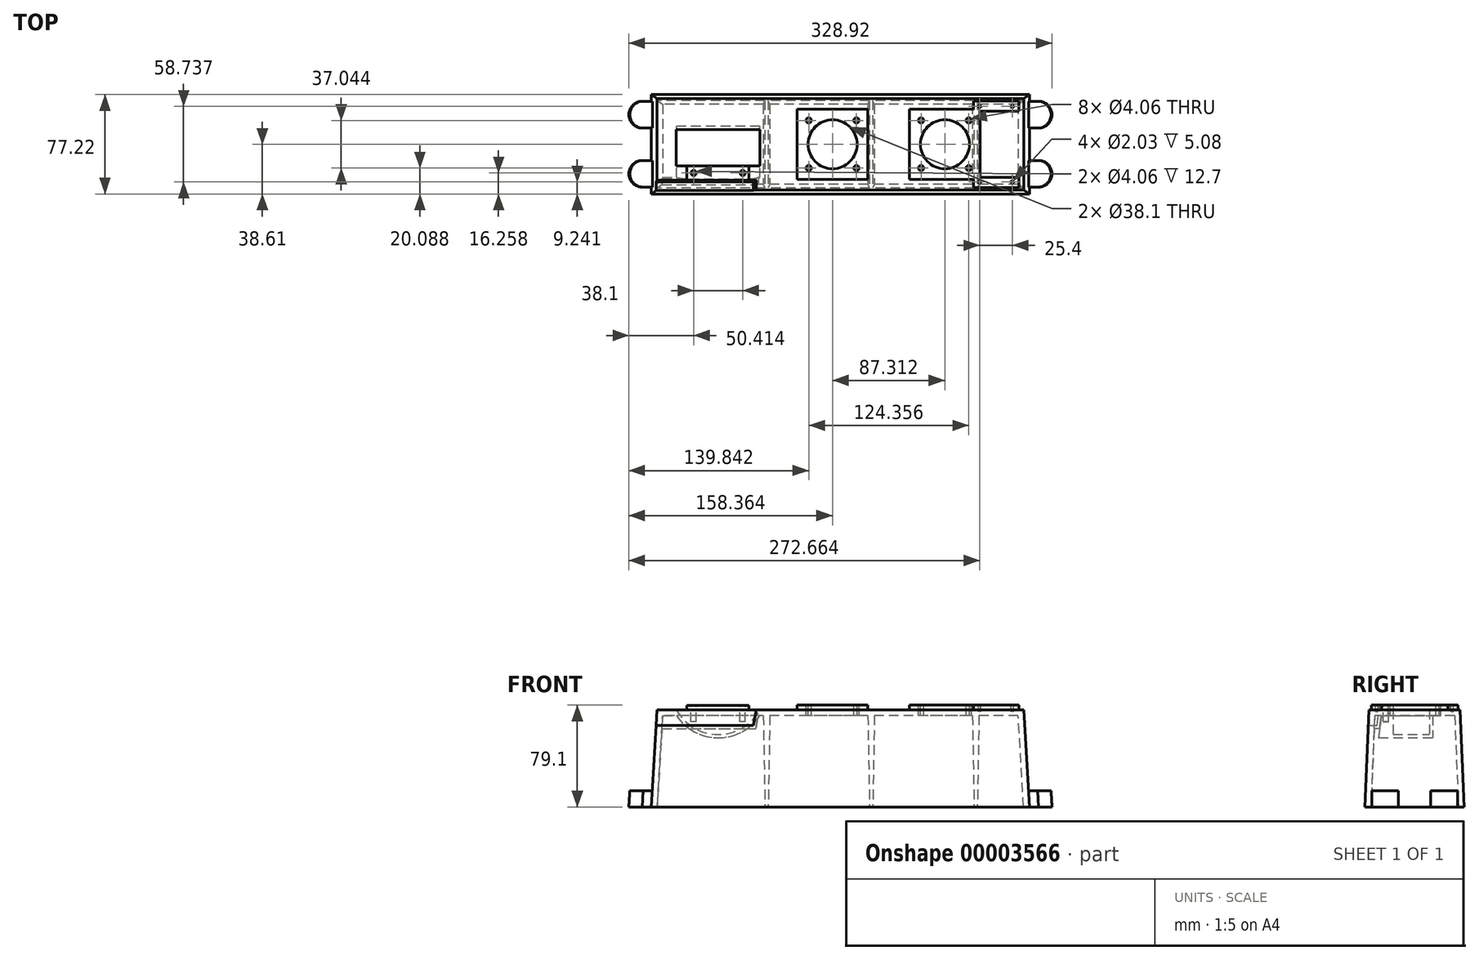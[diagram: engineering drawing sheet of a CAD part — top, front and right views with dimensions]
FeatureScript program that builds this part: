
annotation { "Feature Type Name" : "Feature", "Feature Type Description" : "" }
export const myFeature = defineFeature(function(context is Context, id is Id, definition is map)
    precondition{}
    {
        {
            var Q0;
            Q0=qCreatedBy(makeId("Top.planeOp"),FACE);
            cPlane(context, id + "F0", {"entities" : qUnion([Q0]), "cplaneType" : CPlaneType.OFFSET, "offset" : 75.6 * mm, "width" : 152.4 * mm, "height" : 152.4 * mm});
        }
        {
            var Q0;
            Q0=qCreatedBy(makeId("Top.planeOp"),FACE);
            var sketch = newSketch(context, id + "F1", { "sketchPlane" : qUnion([Q0])});
            skLineSegment(sketch, "E0.rect.bottom", {"start": v(146.94, 38.6) * mm, "end": v(-146.94, 38.6) * mm});
            skLineSegment(sketch, "E0.rect.top", {"start": v(146.94, -38.6) * mm, "end": v(-146.94, -38.6) * mm});
            skLineSegment(sketch, "E0.rect.left", {"start": v(146.94, 38.6) * mm, "end": v(146.94, -38.6) * mm});
            skLineSegment(sketch, "E0.rect.right", {"start": v(-146.94, 38.6) * mm, "end": v(-146.94, -38.6) * mm});
            skPoint(sketch, "E0.rect.middle", {"position": v(0, 0) * mm});
            skSolve(sketch);
        }
        {
            var Q0;
            Q0=qCreatedBy(id+"F0.planeOp",FACE);
            var sketch = newSketch(context, id + "F2", { "sketchPlane" : qUnion([Q0])});
            skLineSegment(sketch, "E1.rect.bottom", {"start": v(142.5, 35.43) * mm, "end": v(-142.5, 35.43) * mm});
            skLineSegment(sketch, "E1.rect.top", {"start": v(142.5, -35.43) * mm, "end": v(-142.5, -35.43) * mm});
            skLineSegment(sketch, "E1.rect.left", {"start": v(142.5, 35.43) * mm, "end": v(142.5, -35.43) * mm});
            skLineSegment(sketch, "E1.rect.right", {"start": v(-142.5, 35.43) * mm, "end": v(-142.5, -35.43) * mm});
            skPoint(sketch, "E1.rect.middle", {"position": v(0, 0) * mm});
            skSolve(sketch);
        }
        {
            var Q0;
            Q0=makeQuery(id+"F1.imprint","IMPRINT",FACE,{"disambiguationData":[TD([[makeQuery(id+"F1.imprint","IMPRINT",EDGE,{"derivedFrom":sQuery(id+"F1.wireOp",EDGE,"E0.rect.bottom")}),1.0]])]});
            var Q1;
            Q1=makeQuery(id+"F2.imprint","IMPRINT",FACE,{"disambiguationData":[TD([[makeQuery(id+"F2.imprint","IMPRINT",EDGE,{"derivedFrom":sQuery(id+"F2.wireOp",EDGE,"E1.rect.bottom")}),1.0]])]});
            loft(context, id + "F3", {"sheetProfilesArray" : [{ "sheetProfileEntities" : qUnion([Q0]) }, { "sheetProfileEntities" : qUnion([Q1]) }]});
        }
        {
            var Q0;
            Q0=makeQuery(id+"F3.opLoft","CAP_FACE",FACE,{"disambiguationData":[OSD([makeQuery(id+"F1.imprint","IMPRINT",FACE,{"disambiguationData":[TD([[makeQuery(id+"F1.imprint","IMPRINT",EDGE,{"derivedFrom":sQuery(id+"F1.wireOp",EDGE,"E0.rect.bottom")}),1.0]])]})])],"isStart":true});
            shell(context, id + "F4", {"entities" : qUnion([Q0]), "thickness" : 4.57 * mm});
        }
        {
            var Q0;
            Q0=makeQuery(id+"F3.opLoft","SWEPT_FACE",FACE,{"disambiguationData":[OSD([sQuery(id+"F1.wireOp",EDGE,"E0.rect.bottom"),sQuery(id+"F1.wireOp",EDGE,"E0.rect.top"),sQuery(id+"F1.wireOp",EDGE,"E0.rect.right"),sQuery(id+"F2.wireOp",EDGE,"E1.rect.bottom"),sQuery(id+"F2.wireOp",EDGE,"E1.rect.top"),sQuery(id+"F2.wireOp",EDGE,"E1.rect.right")])]});
            var sketch = newSketch(context, id + "F5", { "sketchPlane" : qUnion([Q0])});
            skLineSegment(sketch, "E2", {"start": v(-22.99, -8.62) * mm, "end": v(-22.99, 4.08) * mm});
            skLineSegment(sketch, "E3", {"start": v(22.99, -8.62) * mm, "end": v(22.99, 4.08) * mm});
            skSolve(sketch);
        }
        {
            var Q0;
            Q0=qCreatedBy(makeId("Top.planeOp"),FACE);
            var sketch = newSketch(context, id + "F6", { "sketchPlane" : qUnion([Q0])});
            skLineSegment(sketch, "E4.bottom", {"start": v(-146.94, 33.4) * mm, "end": v(-154.05, 33.4) * mm});
            skLineSegment(sketch, "E4.top", {"start": v(-146.94, 12.57) * mm, "end": v(-154.05, 12.57) * mm});
            skLineSegment(sketch, "E4.left", {"start": v(-146.94, 33.4) * mm, "end": v(-146.94, 12.57) * mm});
            skLineSegment(sketch, "E4.right", {"start": v(-164.47, 22.99) * mm, "end": v(-164.47, 22.99) * mm});
            skLineSegment(sketch, "E5.bottom", {"start": v(-146.94, -12.57) * mm, "end": v(-154.05, -12.57) * mm});
            skLineSegment(sketch, "E5.top", {"start": v(-146.94, -33.4) * mm, "end": v(-154.05, -33.4) * mm});
            skLineSegment(sketch, "E5.left", {"start": v(-146.94, -12.57) * mm, "end": v(-146.94, -33.4) * mm});
            skLineSegment(sketch, "E5.right", {"start": v(-164.47, -22.99) * mm, "end": v(-164.47, -22.99) * mm});
            skPoint(sketch, "E6.visualSharp", {"position": v(-164.47, 33.4) * mm});
            skArc(sketch, "E6.filletArc", {"start": v(-154.05, 33.4) * mm, "mid": v(-161.41, 30.35) * mm, "end": v(-164.47, 22.99) * mm});
            skPoint(sketch, "E7.visualSharp", {"position": v(-164.47, 12.57) * mm});
            skArc(sketch, "E7.filletArc", {"start": v(-164.47, 22.99) * mm, "mid": v(-161.41, 15.62) * mm, "end": v(-154.05, 12.57) * mm});
            skPoint(sketch, "E8.visualSharp", {"position": v(-164.47, -12.57) * mm});
            skArc(sketch, "E8.filletArc", {"start": v(-154.05, -12.57) * mm, "mid": v(-161.41, -15.62) * mm, "end": v(-164.47, -22.99) * mm});
            skPoint(sketch, "E9.visualSharp", {"position": v(-164.47, -33.4) * mm});
            skArc(sketch, "E9.filletArc", {"start": v(-164.47, -22.99) * mm, "mid": v(-161.41, -30.35) * mm, "end": v(-154.05, -33.4) * mm});
            skSolve(sketch);
        }
        {
            var Q0;
            Q0=makeQuery(id+"F6.imprint","IMPRINT",FACE,{"disambiguationData":[TD([[makeQuery(id+"F6.imprint","IMPRINT",EDGE,{"derivedFrom":sQuery(id+"F6.wireOp",EDGE,"E4.bottom")}),1.0]])]});
            var Q1;
            Q1=makeQuery(id+"F6.imprint","IMPRINT",FACE,{"disambiguationData":[TD([[makeQuery(id+"F6.imprint","IMPRINT",EDGE,{"derivedFrom":sQuery(id+"F6.wireOp",EDGE,"E5.bottom")}),1.0]])]});
            var Q2;
            Q2=sQuery(id+"F5.wireOp",EDGE,"E2");
            sweep(context, id + "F7", {"operationType" : NewBodyOperationType.ADD, "profiles" : qUnion([Q0, Q1]), "path" : qUnion([Q2])});
        }
        {
            var Q0;
            Q0=makeQuery(id+"F3.opLoft","SWEPT_BODY",BODY,{"disambiguationData":[OSD([makeQuery(id+"F1.imprint","IMPRINT",FACE,{"disambiguationData":[TD([[makeQuery(id+"F1.imprint","IMPRINT",EDGE,{"derivedFrom":sQuery(id+"F1.wireOp",EDGE,"E0.rect.bottom")}),1.0]])]}),makeQuery(id+"F2.imprint","IMPRINT",FACE,{"disambiguationData":[TD([[makeQuery(id+"F2.imprint","IMPRINT",EDGE,{"derivedFrom":sQuery(id+"F2.wireOp",EDGE,"E1.rect.bottom")}),1.0]])]})])]});
            var Q1;
            Q1=qCreatedBy(makeId("Right.planeOp"),FACE);
            mirror(context, id + "F8", {"entities" : qUnion([Q0]), "mirrorPlane" : qUnion([Q1])});
        }
        {
            var Q0;
            Q0=qCreatedBy(id+"F0.planeOp",FACE);
            cPlane(context, id + "F9", {"entities" : qUnion([Q0]), "cplaneType" : CPlaneType.OFFSET, "offset" : 12.14 * mm, "oppositeDirection" : true, "width" : 152.4 * mm, "height" : 152.4 * mm});
        }
        {
            var Q0;
            Q0=qCreatedBy(id+"F9.planeOp",FACE);
            cPlane(context, id + "F10", {"entities" : qUnion([Q0]), "cplaneType" : CPlaneType.OFFSET, "offset" : 2.54 * mm, "oppositeDirection" : true, "width" : 152.4 * mm, "height" : 152.4 * mm});
        }
        {
            var Q0;
            Q0=qCreatedBy(id+"F10.planeOp",FACE);
            var sketch = newSketch(context, id + "F11", { "sketchPlane" : qUnion([Q0])});
            skLineSegment(sketch, "E10.bottom", {"start": v(-143.36, -27.16) * mm, "end": v(-65.89, -27.16) * mm});
            skLineSegment(sketch, "E10.top", {"start": v(-143.36, -36.05) * mm, "end": v(-65.89, -36.05) * mm});
            skLineSegment(sketch, "E10.left", {"start": v(-143.36, -27.16) * mm, "end": v(-143.36, -36.05) * mm});
            skLineSegment(sketch, "E10.right", {"start": v(-65.89, -27.16) * mm, "end": v(-65.89, -36.05) * mm});
            skSolve(sketch);
        }
        {
            var Q0;
            Q0=makeQuery(id+"F3.opLoft","CAP_FACE",FACE,{"disambiguationData":[OSD([makeQuery(id+"F2.imprint","IMPRINT",FACE,{"disambiguationData":[TD([[makeQuery(id+"F2.imprint","IMPRINT",EDGE,{"derivedFrom":sQuery(id+"F2.wireOp",EDGE,"E1.rect.bottom")}),1.0]])]})])],"isStart":true});
            var sketch = newSketch(context, id + "F12", { "sketchPlane" : qUnion([Q0])});
            skLineSegment(sketch, "E11.bottom", {"start": v(-63, -35.43) * mm, "end": v(-142.5, -35.43) * mm});
            skLineSegment(sketch, "E11.top", {"start": v(-63, -25.27) * mm, "end": v(-142.5, -25.27) * mm});
            skLineSegment(sketch, "E11.left", {"start": v(-63, -35.43) * mm, "end": v(-63, -25.27) * mm});
            skLineSegment(sketch, "E11.right", {"start": v(-142.5, -35.43) * mm, "end": v(-142.5, -25.27) * mm});
            skSolve(sketch);
        }
        {
            var Q2;
            Q2=makeQuery(id+"F12.imprint","IMPRINT",FACE,{"disambiguationData":[TD([[makeQuery(id+"F12.imprint","IMPRINT",EDGE,{"derivedFrom":sQuery(id+"F12.wireOp",EDGE,"E11.bottom")}),1.0]])]});
            var Q3;
            Q3 = qSketchRegion(id + "F11", true);
            loft(context, id + "F13", {"operationType" : NewBodyOperationType.ADD, "sheetProfilesArray" : [{ "sheetProfileEntities" : qUnion([Q2]) }, { "sheetProfileEntities" : qUnion([Q3]) }]});
        }
        {
            var Q0;
            Q0=makeQuery(id+"F3.opLoft","CAP_FACE",FACE,{"disambiguationData":[OSD([makeQuery(id+"F2.imprint","IMPRINT",FACE,{"disambiguationData":[TD([[makeQuery(id+"F2.imprint","IMPRINT",EDGE,{"derivedFrom":sQuery(id+"F2.wireOp",EDGE,"E1.rect.bottom")}),1.0]])]})])],"isStart":true});
            var sketch = newSketch(context, id + "F14", { "sketchPlane" : qUnion([Q0])});
            skLineSegment(sketch, "E12.bottom", {"start": v(-65.53, -27.81) * mm, "end": v(-150.84, -27.81) * mm});
            skLineSegment(sketch, "E12.top", {"start": v(-65.53, -43.06) * mm, "end": v(-150.84, -43.06) * mm});
            skLineSegment(sketch, "E12.left", {"start": v(-65.53, -27.81) * mm, "end": v(-65.53, -43.06) * mm});
            skLineSegment(sketch, "E12.right", {"start": v(-150.84, -27.81) * mm, "end": v(-150.84, -43.06) * mm});
            skSolve(sketch);
        }
        {
            var Q0;
            Q0=qCreatedBy(id+"F9.planeOp",FACE);
            var sketch = newSketch(context, id + "F15", { "sketchPlane" : qUnion([Q0])});
            skLineSegment(sketch, "E13.bottom", {"start": v(-67.56, -29.08) * mm, "end": v(-150.57, -29.08) * mm});
            skLineSegment(sketch, "E13.top", {"start": v(-67.56, -49.34) * mm, "end": v(-150.57, -49.34) * mm});
            skLineSegment(sketch, "E13.left", {"start": v(-67.56, -29.08) * mm, "end": v(-67.56, -49.34) * mm});
            skLineSegment(sketch, "E13.right", {"start": v(-150.57, -29.08) * mm, "end": v(-150.57, -49.34) * mm});
            skSolve(sketch);
        }
        {
            var Q1;
            {var subQ3=sQuery(id+"F14.wireOp",EDGE,"E12.left");var subQ7=sQuery(id+"F14.wireOp",EDGE,"E12.bottom");var subQ9=makeQuery(id+"F14.imprint","INTERSECT",VERTEX,{"derivedFrom":[subQ7,subQ3]});Q1=makeQuery(id+"F14.imprint","IMPRINT",FACE,{"disambiguationData":[TD([[makeQuery(id+"F14.imprint","IMPRINT",EDGE,{"disambiguationData":[TD([[subQ9,-1.0]])],"derivedFrom":subQ7}),1.0]])]});}
            var Q2;
            Q2=makeQuery(id+"F15.imprint","IMPRINT",FACE,{"disambiguationData":[TD([[makeQuery(id+"F15.imprint","IMPRINT",EDGE,{"derivedFrom":sQuery(id+"F15.wireOp",EDGE,"E13.bottom")}),1.0]])]});
            loft(context, id + "F16", {"operationType" : NewBodyOperationType.REMOVE, "sheetProfilesArray" : [{ "sheetProfileEntities" : qUnion([Q1]) }, { "sheetProfileEntities" : qUnion([Q2]) }]});
        }
        {
            var Q0;
            Q0=makeQuery(id+"F3.opLoft","CAP_FACE",FACE,{"disambiguationData":[OSD([makeQuery(id+"F2.imprint","IMPRINT",FACE,{"disambiguationData":[TD([[makeQuery(id+"F2.imprint","IMPRINT",EDGE,{"derivedFrom":sQuery(id+"F2.wireOp",EDGE,"E1.rect.bottom")}),1.0]])]})])],"isStart":true});
            var sketch = newSketch(context, id + "F17", { "sketchPlane" : qUnion([Q0])});
            skLineSegment(sketch, "E14.bottom", {"start": v(-119.38, -27.81) * mm, "end": v(-71.12, -27.81) * mm});
            skLineSegment(sketch, "E14.top", {"start": v(-119.38, -16.9) * mm, "end": v(-71.12, -16.9) * mm});
            skLineSegment(sketch, "E14.left", {"start": v(-119.38, -27.81) * mm, "end": v(-119.38, -16.9) * mm});
            skLineSegment(sketch, "E14.right", {"start": v(-71.12, -27.81) * mm, "end": v(-71.12, -16.9) * mm});
            skSolve(sketch);
        }
        {
            var Q0;
            Q0 = qSketchRegion(id + "F17", true);
            extrude(context, id + "F18", {"entities" : qUnion([Q0]), "operationType" : NewBodyOperationType.ADD, "depth" : 3.2 * mm});
        }
        {
            var Q0;
            Q0=makeQuery(id+"F3.opLoft","CAP_FACE",FACE,{"disambiguationData":[OSD([makeQuery(id+"F2.imprint","IMPRINT",FACE,{"disambiguationData":[TD([[makeQuery(id+"F2.imprint","IMPRINT",EDGE,{"derivedFrom":sQuery(id+"F2.wireOp",EDGE,"E1.rect.bottom")}),1.0]])]})])],"isStart":true});
            var sketch = newSketch(context, id + "F19", { "sketchPlane" : qUnion([Q0])});
            skLineSegment(sketch, "E15.bottom", {"start": v(-127.5, -16.9) * mm, "end": v(-62.48, -16.9) * mm});
            skLineSegment(sketch, "E15.top", {"start": v(-127.5, 11.56) * mm, "end": v(-62.48, 11.56) * mm});
            skLineSegment(sketch, "E15.left", {"start": v(-127.5, -16.9) * mm, "end": v(-127.5, 11.56) * mm});
            skLineSegment(sketch, "E15.right", {"start": v(-62.48, -16.9) * mm, "end": v(-62.48, 11.56) * mm});
            skSolve(sketch);
        }
        {
            var Q0;
            Q0=sQuery(id+"F19.wireOp",EDGE,"E15.top");
            cPlane(context, id + "F20", {"entities" : qUnion([Q0]), "cplaneType" : CPlaneType.LINE_ANGLE, "offset" : 152.4 * mm, "angle" : 0 * degree, "width" : 152.4 * mm, "height" : 152.4 * mm});
        }
        {
            var Q0;
            Q0=qCreatedBy(id+"F20.planeOp",FACE);
            var sketch = newSketch(context, id + "F21", { "sketchPlane" : qUnion([Q0])});
            skArc(sketch, "E16", {"start": v(59.94, 75.6) * mm, "mid": v(95, 53.76) * mm, "end": v(130.05, 75.6) * mm});
            skLineSegment(sketch, "E17", {"start": v(59.94, 75.6) * mm, "end": v(130.05, 75.6) * mm});
            skSolve(sketch);
        }
        {
            var Q0;
            Q0 = qSketchRegion(id + "F21", true);
            var Q1;
            Q1=makeQuery(id+"F13.opLoft","SWEPT_FACE",FACE,{"disambiguationData":[OSD([sQuery(id+"F2.wireOp",EDGE,"E1.rect.bottom"),sQuery(id+"F2.wireOp",EDGE,"E1.rect.top"),sQuery(id+"F2.wireOp",EDGE,"E1.rect.right"),sQuery(id+"F11.wireOp",EDGE,"E10.bottom"),sQuery(id+"F11.wireOp",EDGE,"E10.left"),sQuery(id+"F11.wireOp",EDGE,"E10.right"),sQuery(id+"F12.wireOp",EDGE,"E11.top"),sQuery(id+"F12.wireOp",EDGE,"E11.left"),sQuery(id+"F12.wireOp",EDGE,"E11.right")])]});
            extrude(context, id + "F22", {"entities" : qUnion([Q0]), "operationType" : NewBodyOperationType.ADD, "endBound" : BoundingType.UP_TO_SURFACE, "oppositeDirection" : true, "endBoundEntityFace" : qUnion([Q1]), "depth" : 25.4 * mm, "hasSecondDirection" : true, "secondDirectionOppositeDirection" : false, "secondDirectionDepth" : 2.54 * mm});
        }
        {
            var Q0;
            Q0=qCreatedBy(id+"F20.planeOp",FACE);
            var sketch = newSketch(context, id + "F23", { "sketchPlane" : qUnion([Q0])});
            skArc(sketch, "E18", {"start": v(62.48, 75.6) * mm, "mid": v(95, 56.3) * mm, "end": v(127.5, 75.6) * mm});
            skLineSegment(sketch, "E19", {"start": v(62.48, 75.6) * mm, "end": v(127.5, 75.6) * mm});
            skSolve(sketch);
        }
        {
            var Q0;
            Q0 = qSketchRegion(id + "F23", true);
            var Q1;
            Q1=makeQuery(id+"F18.opExtrude","SWEPT_FACE",FACE,{"disambiguationData":[OSD([sQuery(id+"F17.wireOp",EDGE,"E14.top")])]});
            extrude(context, id + "F24", {"entities" : qUnion([Q0]), "operationType" : NewBodyOperationType.REMOVE, "endBound" : BoundingType.UP_TO_SURFACE, "oppositeDirection" : true, "endBoundEntityFace" : qUnion([Q1]), "depth" : 25.4 * mm});
        }
        {
            var Q0;
            Q0=makeQuery(id+"F19.imprint","IMPRINT",FACE,{"disambiguationData":[TD([[makeQuery(id+"F19.imprint","IMPRINT",EDGE,{"derivedFrom":sQuery(id+"F19.wireOp",EDGE,"E15.top")}),1.0]])]});
            var sketch = newSketch(context, id + "F25", { "sketchPlane" : qUnion([Q0])});
            skLineSegment(sketch, "E20", {"start": v(-6.1, -35.43) * mm, "end": v(-6.1, 35.43) * mm, "construction": true});
            skLineSegment(sketch, "E21", {"start": v(-95, 11.56) * mm, "end": v(-95, -16.9) * mm});
            skLineSegment(sketch, "E22.rect.bottom", {"start": v(-33.53, -27.43) * mm, "end": v(21.34, -27.43) * mm});
            skLineSegment(sketch, "E22.rect.top", {"start": v(-33.53, 27.43) * mm, "end": v(21.34, 27.43) * mm});
            skLineSegment(sketch, "E22.rect.left", {"start": v(-33.53, -27.43) * mm, "end": v(-33.53, 27.43) * mm});
            skLineSegment(sketch, "E22.rect.right", {"start": v(21.34, -27.43) * mm, "end": v(21.34, 27.43) * mm});
            skPoint(sketch, "E22.rect.middle", {"position": v(-6.1, 0) * mm});
            skCircle(sketch, "E23", {"center": v(-6.1, 0) * mm, "radius": 26.2 * mm, "construction": true});
            skSolve(sketch);
        }
        {
            var Q0;
            Q0 = qSketchRegion(id + "F25", true);
            extrude(context, id + "F26", {"entities" : qUnion([Q0]), "operationType" : NewBodyOperationType.ADD, "depth" : 3.5 * mm});
        }
        {
            var Q0;
            Q0=makeQuery(id+"F19.imprint","IMPRINT",FACE,{"disambiguationData":[TD([[makeQuery(id+"F19.imprint","IMPRINT",EDGE,{"derivedFrom":sQuery(id+"F19.wireOp",EDGE,"E15.top")}),1.0]])]});
            var sketch = newSketch(context, id + "F27", { "sketchPlane" : qUnion([Q0])});
            skLineSegment(sketch, "E24", {"start": v(0, 0) * mm, "end": v(142.5, 0) * mm, "construction": true});
            skLineSegment(sketch, "E25.rect.bottom", {"start": v(53.78, -27.43) * mm, "end": v(103.57, -27.43) * mm});
            skLineSegment(sketch, "E25.rect.top", {"start": v(53.78, 27.43) * mm, "end": v(103.57, 27.43) * mm});
            skLineSegment(sketch, "E25.rect.left", {"start": v(53.78, -27.43) * mm, "end": v(53.78, 27.43) * mm});
            skLineSegment(sketch, "E25.rect.right", {"start": v(108.65, -25.78) * mm, "end": v(108.65, 25.78) * mm});
            skPoint(sketch, "E25.rect.middle", {"position": v(81.22, 0) * mm});
            skLineSegment(sketch, "E26", {"start": v(-6.1, 0) * mm, "end": v(-6.1, -27.43) * mm, "construction": true});
            skLineSegment(sketch, "E27", {"start": v(103.57, -27.43) * mm, "end": v(103.57, -33.65) * mm});
            skLineSegment(sketch, "E28", {"start": v(103.57, -33.65) * mm, "end": v(138.62, -33.65) * mm});
            skLineSegment(sketch, "E29", {"start": v(138.62, -33.65) * mm, "end": v(138.62, -25.78) * mm});
            skLineSegment(sketch, "E30", {"start": v(138.62, -25.78) * mm, "end": v(108.65, -25.78) * mm});
            skLineSegment(sketch, "E31", {"start": v(103.57, 27.43) * mm, "end": v(103.57, 33.65) * mm});
            skLineSegment(sketch, "E32", {"start": v(103.57, 33.65) * mm, "end": v(138.62, 33.65) * mm});
            skLineSegment(sketch, "E33", {"start": v(138.62, 33.65) * mm, "end": v(138.62, 25.78) * mm});
            skLineSegment(sketch, "E34", {"start": v(138.62, 25.78) * mm, "end": v(108.65, 25.78) * mm});
            skPoint(sketch, "E35.orphan", {"position": v(108.65, -27.43) * mm});
            skPoint(sketch, "E36.orphan", {"position": v(108.65, 27.43) * mm});
            skSolve(sketch);
        }
        {
            var Q0;
            Q0 = qSketchRegion(id + "F27", true);
            extrude(context, id + "F28", {"entities" : qUnion([Q0]), "operationType" : NewBodyOperationType.ADD, "depth" : 3.5 * mm});
        }
        {
            var Q0;
            Q0=makeQuery(id+"F18.opExtrude","CAP_FACE",FACE,{"disambiguationData":[OSD([sQuery(id+"F17.wireOp",EDGE,"E14.bottom"),sQuery(id+"F17.wireOp",EDGE,"E14.top"),sQuery(id+"F17.wireOp",EDGE,"E14.left"),sQuery(id+"F17.wireOp",EDGE,"E14.right")])],"isStart":false});
            var sketch = newSketch(context, id + "F29", { "sketchPlane" : qUnion([Q0])});
            skLineSegment(sketch, "E37", {"start": v(-6.1, -27.43) * mm, "end": v(-6.1, 11.56) * mm, "construction": true});
            skLineSegment(sketch, "E38", {"start": v(-6.1, 11.56) * mm, "end": v(-95, 11.56) * mm, "construction": true});
            skLineSegment(sketch, "E39", {"start": v(-95, 11.56) * mm, "end": v(-95, -27.81) * mm, "construction": true});
            skLineSegment(sketch, "E40", {"start": v(-95, -27.81) * mm, "end": v(-95, -16.9) * mm, "construction": true});
            skLineSegment(sketch, "E41", {"start": v(-95, -22.35) * mm, "end": v(-75.95, -22.35) * mm, "construction": true});
            skLineSegment(sketch, "E42", {"start": v(-95, -22.35) * mm, "end": v(-114.05, -22.35) * mm, "construction": true});
            skCircle(sketch, "E43", {"center": v(-75.95, -22.35) * mm, "radius": 2.03 * mm});
            skCircle(sketch, "E44", {"center": v(-114.05, -22.35) * mm, "radius": 2.03 * mm});
            skSolve(sketch);
        }
        {
            var Q0;
            Q0=makeQuery(id+"F29.imprint","IMPRINT",FACE,{"disambiguationData":[TD([[makeQuery(id+"F29.imprint","IMPRINT",EDGE,{"derivedFrom":sQuery(id+"F29.wireOp",EDGE,"E43")}),1.0]])]});
            var Q1;
            Q1=makeQuery(id+"F29.imprint","IMPRINT",FACE,{"disambiguationData":[TD([[makeQuery(id+"F29.imprint","IMPRINT",EDGE,{"derivedFrom":sQuery(id+"F29.wireOp",EDGE,"E44")}),1.0]])]});
            extrude(context, id + "F30", {"entities" : qUnion([Q0, Q1]), "operationType" : NewBodyOperationType.REMOVE, "oppositeDirection" : true, "depth" : 12.7 * mm});
        }
        {
            var Q0;
            Q0=makeQuery(id+"F28.opExtrude","CAP_FACE",FACE,{"disambiguationData":[OSD([sQuery(id+"F27.wireOp",EDGE,"E25.rect.bottom"),sQuery(id+"F27.wireOp",EDGE,"E25.rect.top"),sQuery(id+"F27.wireOp",EDGE,"E25.rect.left"),sQuery(id+"F27.wireOp",EDGE,"E25.rect.right"),sQuery(id+"F27.wireOp",EDGE,"E27"),sQuery(id+"F27.wireOp",EDGE,"E28"),sQuery(id+"F27.wireOp",EDGE,"E29"),sQuery(id+"F27.wireOp",EDGE,"E30"),sQuery(id+"F27.wireOp",EDGE,"E31"),sQuery(id+"F27.wireOp",EDGE,"E32"),sQuery(id+"F27.wireOp",EDGE,"E33"),sQuery(id+"F27.wireOp",EDGE,"E34")])],"isStart":false});
            var sketch = newSketch(context, id + "F31", { "sketchPlane" : qUnion([Q0])});
            skLineSegment(sketch, "E45", {"start": v(108.65, 0) * mm, "end": v(53.78, 0) * mm, "construction": true});
            skLineSegment(sketch, "E46.trimOffspring", {"start": v(21.34, 0) * mm, "end": v(-33.53, 0) * mm, "construction": true});
            skPoint(sketch, "E47.orphan", {"position": v(53.78, -27.43) * mm});
            skPoint(sketch, "E48.0.end.orphan", {"position": v(53.78, 27.43) * mm});
            skPoint(sketch, "E49.orphan", {"position": v(21.34, 27.43) * mm});
            skPoint(sketch, "E48.1.start.orphan", {"position": v(21.34, -27.43) * mm});
            skCircle(sketch, "E50", {"center": v(81.22, 0) * mm, "radius": 19.05 * mm});
            skCircle(sketch, "E51", {"center": v(-6.1, 0) * mm, "radius": 19.05 * mm});
            skSolve(sketch);
        }
        {
            var Q0;
            Q0 = qSketchRegion(id + "F31", true);
            extrude(context, id + "F32", {"entities" : qUnion([Q0]), "operationType" : NewBodyOperationType.REMOVE, "endBound" : BoundingType.THROUGH_ALL, "oppositeDirection" : true, "depth" : 25.4 * mm});
        }
        {
            var Q0;
            Q0=makeQuery(id+"F4.opShell","OFFSET_FACE",FACE,{"disambiguationData":[OSD([makeQuery(id+"F2.imprint","IMPRINT",FACE,{"disambiguationData":[TD([[makeQuery(id+"F2.imprint","IMPRINT",EDGE,{"derivedFrom":sQuery(id+"F2.wireOp",EDGE,"E1.rect.bottom")}),1.0]])]})])]});
            var sketch = newSketch(context, id + "F33", { "sketchPlane" : qUnion([Q0])});
            skLineSegment(sketch, "E52.bottom", {"start": v(107.7, -31.05) * mm, "end": v(102.62, -31.05) * mm});
            skLineSegment(sketch, "E52.top", {"start": v(107.7, 31.05) * mm, "end": v(102.62, 31.05) * mm});
            skLineSegment(sketch, "E52.left", {"start": v(107.7, -31.05) * mm, "end": v(107.7, 31.05) * mm});
            skLineSegment(sketch, "E52.right", {"start": v(102.62, -31.05) * mm, "end": v(102.62, 31.05) * mm});
            skLineSegment(sketch, "E53", {"start": v(105.16, -31.05) * mm, "end": v(105.16, 31.05) * mm, "construction": true});
            skLineSegment(sketch, "E54.1.0.0", {"start": v(21.34, -31.05) * mm, "end": v(21.34, 31.05) * mm});
            skLineSegment(sketch, "E54.1.0.1", {"start": v(26.42, -31.05) * mm, "end": v(21.34, -31.05) * mm});
            skLineSegment(sketch, "E54.1.0.2", {"start": v(26.42, -31.05) * mm, "end": v(26.42, 31.05) * mm});
            skLineSegment(sketch, "E54.1.0.3", {"start": v(26.42, 31.05) * mm, "end": v(21.34, 31.05) * mm});
            skLineSegment(sketch, "E54.2.0.0", {"start": v(-59.94, -31.05) * mm, "end": v(-59.94, 31.05) * mm});
            skLineSegment(sketch, "E54.2.0.1", {"start": v(-54.86, -31.05) * mm, "end": v(-59.94, -31.05) * mm});
            skLineSegment(sketch, "E54.2.0.2", {"start": v(-54.86, -31.05) * mm, "end": v(-54.86, 31.05) * mm});
            skLineSegment(sketch, "E54.2.0.3", {"start": v(-54.86, 31.05) * mm, "end": v(-59.94, 31.05) * mm});
            skLineSegment(sketch, "E54.direction1", {"start": v(102.62, -31.05) * mm, "end": v(21.34, -31.05) * mm, "construction": true});
            skSolve(sketch);
        }
        {
            var Q0;
            {var subQ0=sQuery(id+"F5.wireOp",VERTEX,"E2.start");var subQ1=makeQuery(id+"F7.boolean.opBoolean","MERGE",FACE,{"derivedFrom":[makeQuery(id+"F3.opLoft","CAP_FACE",FACE,{"disambiguationData":[OSD([makeQuery(id+"F1.imprint","IMPRINT",FACE,{"disambiguationData":[TD([[makeQuery(id+"F1.imprint","IMPRINT",EDGE,{"derivedFrom":sQuery(id+"F1.wireOp",EDGE,"E0.rect.bottom")}),1.0]])]})])],"isStart":true}),makeQuery(id+"F7.opSweep","CAP_FACE",FACE,{"disambiguationData":[OSD([subQ0,sQuery(id+"F6.wireOp",EDGE,"E4.bottom"),sQuery(id+"F6.wireOp",EDGE,"E4.top"),sQuery(id+"F6.wireOp",EDGE,"E4.left"),sQuery(id+"F6.wireOp",EDGE,"E6.filletArc"),sQuery(id+"F6.wireOp",EDGE,"E7.filletArc")])],"isStart":true}),makeQuery(id+"F7.opSweep","CAP_FACE",FACE,{"disambiguationData":[OSD([subQ0,sQuery(id+"F6.wireOp",EDGE,"E5.bottom"),sQuery(id+"F6.wireOp",EDGE,"E5.top"),sQuery(id+"F6.wireOp",EDGE,"E5.left"),sQuery(id+"F6.wireOp",EDGE,"E8.filletArc"),sQuery(id+"F6.wireOp",EDGE,"E9.filletArc")])],"isStart":true})]});Q0=makeQuery(id+"F13.boolean.opBoolean","MERGE",FACE,{"derivedFrom":[subQ1,makeQuery(id+"F8.opPattern","COPY",FACE,{"derivedFrom":subQ1,"instanceName":"1"})]});}
            var sketch = newSketch(context, id + "F34", { "sketchPlane" : qUnion([Q0])});
            skLineSegment(sketch, "E55.bottom", {"start": v(106.43, -34.03) * mm, "end": v(103.9, -34.03) * mm});
            skLineSegment(sketch, "E55.top", {"start": v(106.43, 34.03) * mm, "end": v(103.9, 34.03) * mm});
            skLineSegment(sketch, "E55.left", {"start": v(106.43, -34.03) * mm, "end": v(106.43, 34.03) * mm});
            skLineSegment(sketch, "E55.right", {"start": v(103.9, -34.03) * mm, "end": v(103.9, 34.03) * mm});
            skLineSegment(sketch, "E56", {"start": v(105.16, -34.03) * mm, "end": v(105.16, 34.03) * mm, "construction": true});
            skLineSegment(sketch, "E57.1.0.0", {"start": v(22.61, -34.03) * mm, "end": v(22.61, 34.03) * mm});
            skLineSegment(sketch, "E57.1.0.1", {"start": v(25.15, -34.03) * mm, "end": v(22.61, -34.03) * mm});
            skLineSegment(sketch, "E57.1.0.2", {"start": v(25.15, -34.03) * mm, "end": v(25.15, 34.03) * mm});
            skLineSegment(sketch, "E57.1.0.3", {"start": v(25.15, 34.03) * mm, "end": v(22.61, 34.03) * mm});
            skLineSegment(sketch, "E57.2.0.0", {"start": v(-58.67, -34.03) * mm, "end": v(-58.67, 34.03) * mm});
            skLineSegment(sketch, "E57.2.0.1", {"start": v(-56.13, -34.03) * mm, "end": v(-58.67, -34.03) * mm});
            skLineSegment(sketch, "E57.2.0.2", {"start": v(-56.13, -34.03) * mm, "end": v(-56.13, 34.03) * mm});
            skLineSegment(sketch, "E57.2.0.3", {"start": v(-56.13, 34.03) * mm, "end": v(-58.67, 34.03) * mm});
            skLineSegment(sketch, "E57.direction1", {"start": v(103.9, -34.03) * mm, "end": v(22.61, -34.03) * mm, "construction": true});
            skSolve(sketch);
        }
        {
            var Q1;
            Q1=makeQuery(id+"F33.imprint","IMPRINT",FACE,{"disambiguationData":[TD([[makeQuery(id+"F33.imprint","IMPRINT",EDGE,{"derivedFrom":sQuery(id+"F33.wireOp",EDGE,"E52.bottom")}),-1.0]])]});
            var Q2;
            Q2=makeQuery(id+"F34.imprint","IMPRINT",FACE,{"disambiguationData":[TD([[makeQuery(id+"F34.imprint","IMPRINT",EDGE,{"derivedFrom":sQuery(id+"F34.wireOp",EDGE,"E55.bottom")}),-1.0]])]});
            loft(context, id + "F35", {"operationType" : NewBodyOperationType.ADD, "sheetProfilesArray" : [{ "sheetProfileEntities" : qUnion([Q1]) }, { "sheetProfileEntities" : qUnion([Q2]) }]});
        }
        {
            var Q1;
            Q1=makeQuery(id+"F33.imprint","IMPRINT",FACE,{"disambiguationData":[TD([[makeQuery(id+"F33.imprint","IMPRINT",EDGE,{"derivedFrom":sQuery(id+"F33.wireOp",EDGE,"E54.1.0.0")}),-1.0]])]});
            var Q2;
            Q2=makeQuery(id+"F34.imprint","IMPRINT",FACE,{"disambiguationData":[TD([[makeQuery(id+"F34.imprint","IMPRINT",EDGE,{"derivedFrom":sQuery(id+"F34.wireOp",EDGE,"E57.1.0.0")}),-1.0]])]});
            loft(context, id + "F36", {"operationType" : NewBodyOperationType.ADD, "sheetProfilesArray" : [{ "sheetProfileEntities" : qUnion([Q1]) }, { "sheetProfileEntities" : qUnion([Q2]) }]});
        }
        {
            var Q1;
            Q1=makeQuery(id+"F33.imprint","IMPRINT",FACE,{"disambiguationData":[TD([[makeQuery(id+"F33.imprint","IMPRINT",EDGE,{"derivedFrom":sQuery(id+"F33.wireOp",EDGE,"E54.2.0.0")}),-1.0]])]});
            var Q2;
            Q2=makeQuery(id+"F34.imprint","IMPRINT",FACE,{"disambiguationData":[TD([[makeQuery(id+"F34.imprint","IMPRINT",EDGE,{"derivedFrom":sQuery(id+"F34.wireOp",EDGE,"E57.2.0.0")}),-1.0]])]});
            loft(context, id + "F37", {"operationType" : NewBodyOperationType.ADD, "sheetProfilesArray" : [{ "sheetProfileEntities" : qUnion([Q1]) }, { "sheetProfileEntities" : qUnion([Q2]) }]});
        }
        {
            var Q0;
            Q0=makeQuery(id+"F26.opExtrude","CAP_FACE",FACE,{"disambiguationData":[OSD([sQuery(id+"F25.wireOp",EDGE,"E22.rect.bottom"),sQuery(id+"F25.wireOp",EDGE,"E22.rect.top"),sQuery(id+"F25.wireOp",EDGE,"E22.rect.left"),sQuery(id+"F25.wireOp",EDGE,"E22.rect.right")])],"isStart":false});
            var sketch = newSketch(context, id + "F38", { "sketchPlane" : qUnion([Q0])});
            skCircle(sketch, "E58", {"center": v(-6.1, 0) * mm, "radius": 26.2 * mm, "construction": true});
            skLineSegment(sketch, "E59", {"start": v(21.34, -27.43) * mm, "end": v(-33.53, 27.43) * mm, "construction": true});
            skLineSegment(sketch, "E60", {"start": v(-33.53, -27.43) * mm, "end": v(21.34, 27.43) * mm, "construction": true});
            skLineSegment(sketch, "E61", {"start": v(53.78, 27.43) * mm, "end": v(108.65, -27.43) * mm, "construction": true});
            skLineSegment(sketch, "E62", {"start": v(53.78, -27.43) * mm, "end": v(108.65, 27.43) * mm, "construction": true});
            skCircle(sketch, "E63", {"center": v(81.22, 0) * mm, "radius": 26.2 * mm, "construction": true});
            skCircle(sketch, "E64", {"center": v(99.74, -18.52) * mm, "radius": 2.03 * mm});
            skCircle(sketch, "E65", {"center": v(62.7, -18.52) * mm, "radius": 2.03 * mm});
            skCircle(sketch, "E66", {"center": v(12.43, -18.52) * mm, "radius": 2.03 * mm});
            skCircle(sketch, "E67", {"center": v(-24.62, -18.52) * mm, "radius": 2.03 * mm});
            skCircle(sketch, "E68", {"center": v(-24.62, 18.52) * mm, "radius": 2.03 * mm});
            skCircle(sketch, "E69", {"center": v(12.43, 18.52) * mm, "radius": 2.03 * mm});
            skCircle(sketch, "E70", {"center": v(62.7, 18.52) * mm, "radius": 2.03 * mm});
            skCircle(sketch, "E71", {"center": v(99.74, 18.52) * mm, "radius": 2.03 * mm});
            skSolve(sketch);
        }
        {
            var Q0;
            Q0 = qSketchRegion(id + "F38", true);
            extrude(context, id + "F39", {"entities" : qUnion([Q0]), "operationType" : NewBodyOperationType.REMOVE, "endBound" : BoundingType.UP_TO_NEXT, "oppositeDirection" : true, "depth" : 25.4 * mm});
        }
        {
            var Q0;
            Q0=makeQuery(id+"F28.opExtrude","CAP_FACE",FACE,{"disambiguationData":[OSD([sQuery(id+"F27.wireOp",EDGE,"E25.rect.bottom"),sQuery(id+"F27.wireOp",EDGE,"E25.rect.top"),sQuery(id+"F27.wireOp",EDGE,"E25.rect.left"),sQuery(id+"F27.wireOp",EDGE,"E25.rect.right"),sQuery(id+"F27.wireOp",EDGE,"E27"),sQuery(id+"F27.wireOp",EDGE,"E28"),sQuery(id+"F27.wireOp",EDGE,"E29"),sQuery(id+"F27.wireOp",EDGE,"E30"),sQuery(id+"F27.wireOp",EDGE,"E31"),sQuery(id+"F27.wireOp",EDGE,"E32"),sQuery(id+"F27.wireOp",EDGE,"E33"),sQuery(id+"F27.wireOp",EDGE,"E34")])],"isStart":false});
            var sketch = newSketch(context, id + "F40", { "sketchPlane" : qUnion([Q0])});
            skLineSegment(sketch, "E72", {"start": v(138.62, -29.37) * mm, "end": v(103.57, -29.37) * mm, "construction": true});
            skLineSegment(sketch, "E73", {"start": v(138.62, 29.37) * mm, "end": v(103.57, 29.37) * mm, "construction": true});
            skLineSegment(sketch, "E74", {"start": v(81.22, 0) * mm, "end": v(142.5, 0) * mm, "construction": true});
            skLineSegment(sketch, "E75", {"start": v(120.9, -29.37) * mm, "end": v(120.9, 29.37) * mm, "construction": true});
            skCircle(sketch, "E76", {"center": v(133.6, -29.37) * mm, "radius": 1.02 * mm});
            skCircle(sketch, "E77", {"center": v(108.2, -29.37) * mm, "radius": 1.02 * mm});
            skCircle(sketch, "E78", {"center": v(108.2, 29.37) * mm, "radius": 1.02 * mm});
            skCircle(sketch, "E79", {"center": v(133.6, 29.37) * mm, "radius": 1.02 * mm});
            skSolve(sketch);
        }
        {
            var Q0;
            Q0 = qSketchRegion(id + "F40", true);
            extrude(context, id + "F41", {"entities" : qUnion([Q0]), "operationType" : NewBodyOperationType.REMOVE, "oppositeDirection" : true, "depth" : 5.08 * mm});
        }
    });
